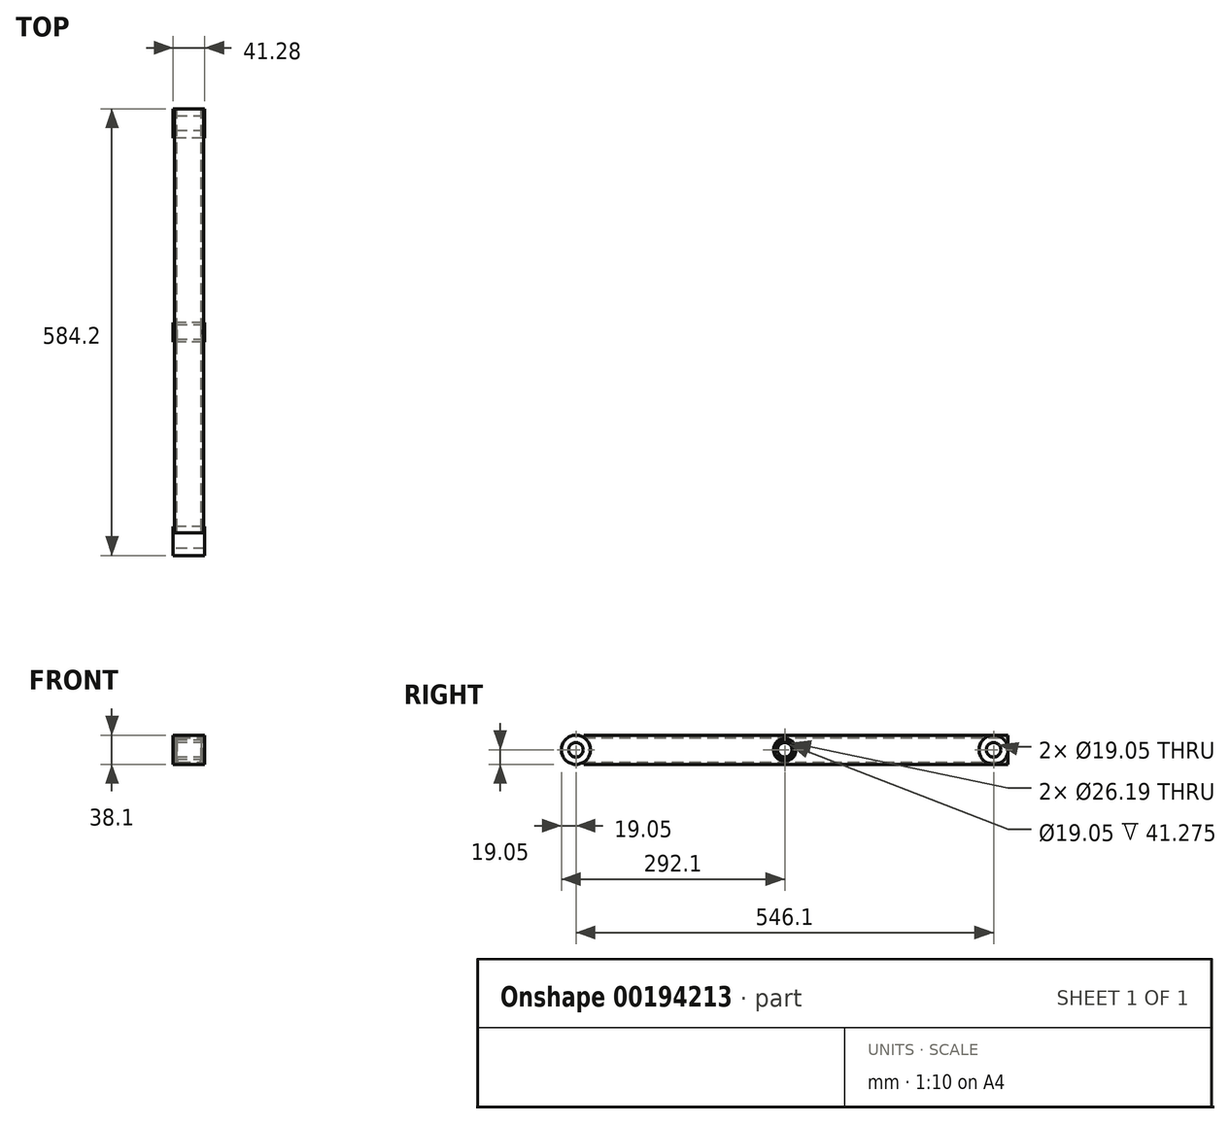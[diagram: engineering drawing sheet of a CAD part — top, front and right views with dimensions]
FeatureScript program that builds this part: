
annotation { "Feature Type Name" : "Feature", "Feature Type Description" : "" }
export const myFeature = defineFeature(function(context is Context, id is Id, definition is map)
    precondition{}
    {
        {
            var Q0;
            Q0=qCreatedBy(makeId("Front.planeOp"),FACE);
            var sketch = newSketch(context, id + "F0", { "sketchPlane" : qUnion([Q0])});
            skLineSegment(sketch, "E0.bottom", {"start": v(-19.05, 19.05) * mm, "end": v(19.05, 19.05) * mm});
            skLineSegment(sketch, "E0.top", {"start": v(-19.05, -19.05) * mm, "end": v(19.05, -19.05) * mm});
            skLineSegment(sketch, "E0.left", {"start": v(-19.05, 19.05) * mm, "end": v(-19.05, -19.05) * mm});
            skLineSegment(sketch, "E0.right", {"start": v(19.05, 19.05) * mm, "end": v(19.05, -19.05) * mm});
            skPoint(sketch, "E0.middle", {"position": v(0, 0) * mm});
            skLineSegment(sketch, "E1.bottom", {"start": v(-15.88, 15.88) * mm, "end": v(15.88, 15.88) * mm});
            skLineSegment(sketch, "E1.top", {"start": v(-15.88, -15.88) * mm, "end": v(15.88, -15.88) * mm});
            skLineSegment(sketch, "E1.left", {"start": v(-15.88, 15.88) * mm, "end": v(-15.88, -15.88) * mm});
            skLineSegment(sketch, "E1.right", {"start": v(15.88, 15.88) * mm, "end": v(15.88, -15.88) * mm});
            skSolve(sketch);
        }
        {
            var Q0;
            Q0=makeQuery(id+"F0.imprint","IMPRINT",FACE,{"disambiguationData":[TD([[makeQuery(id+"F0.imprint","IMPRINT",EDGE,{"derivedFrom":sQuery(id+"F0.wireOp",EDGE,"E0.bottom")}),-1.0]])]});
            extrude(context, id + "F1", {"entities" : qUnion([Q0]), "endBound" : BoundingType.SYMMETRIC, "depth" : 584.2 * mm});
        }
        {
            var Q0;
            Q0=makeQuery(id+"F1.opExtrude","SWEPT_EDGE",EDGE,{"disambiguationData":[OSD([sQuery(id+"F0.wireOp",EDGE,"E1.top"),sQuery(id+"F0.wireOp",EDGE,"E1.left")])]});
            var Q1;
            Q1=makeQuery(id+"F1.opExtrude","SWEPT_EDGE",EDGE,{"disambiguationData":[OSD([sQuery(id+"F0.wireOp",EDGE,"E1.top"),sQuery(id+"F0.wireOp",EDGE,"E1.right")])]});
            var Q2;
            Q2=makeQuery(id+"F1.opExtrude","SWEPT_EDGE",EDGE,{"disambiguationData":[OSD([sQuery(id+"F0.wireOp",EDGE,"E1.bottom"),sQuery(id+"F0.wireOp",EDGE,"E1.right")])]});
            var Q3;
            Q3=makeQuery(id+"F1.opExtrude","SWEPT_EDGE",EDGE,{"disambiguationData":[OSD([sQuery(id+"F0.wireOp",EDGE,"E1.bottom"),sQuery(id+"F0.wireOp",EDGE,"E1.left")])]});
            fillet(context, id + "F2", {"entities" : qUnion([Q0, Q1, Q2, Q3]), "radius" : 3.17 * mm, "tangentPropagation" : true, "allowEdgeOverflow" : false});
        }
        {
            var Q0;
            Q0=makeQuery(id+"F1.opExtrude","SWEPT_EDGE",EDGE,{"disambiguationData":[OSD([sQuery(id+"F0.wireOp",EDGE,"E0.top"),sQuery(id+"F0.wireOp",EDGE,"E0.left")])]});
            var Q1;
            Q1=makeQuery(id+"F1.opExtrude","SWEPT_EDGE",EDGE,{"disambiguationData":[OSD([sQuery(id+"F0.wireOp",EDGE,"E0.top"),sQuery(id+"F0.wireOp",EDGE,"E0.right")])]});
            var Q2;
            Q2=makeQuery(id+"F1.opExtrude","SWEPT_EDGE",EDGE,{"disambiguationData":[OSD([sQuery(id+"F0.wireOp",EDGE,"E0.bottom"),sQuery(id+"F0.wireOp",EDGE,"E0.right")])]});
            var Q3;
            Q3=makeQuery(id+"F1.opExtrude","SWEPT_EDGE",EDGE,{"disambiguationData":[OSD([sQuery(id+"F0.wireOp",EDGE,"E0.bottom"),sQuery(id+"F0.wireOp",EDGE,"E0.left")])]});
            fillet(context, id + "F3", {"entities" : qUnion([Q0, Q1, Q2, Q3]), "radius" : 6.35 * mm, "tangentPropagation" : true, "allowEdgeOverflow" : false});
        }
        {
            var Q0;
            Q0=qCreatedBy(makeId("Top.planeOp"),FACE);
            var sketch = newSketch(context, id + "F4", { "sketchPlane" : qUnion([Q0])});
            skLineSegment(sketch, "E2", {"start": v(-25.89, 0) * mm, "end": v(26.93, 0) * mm, "construction": true});
            skLineSegment(sketch, "E3", {"start": v(-19.05, 0) * mm, "end": v(19.05, 0) * mm});
            skLineSegment(sketch, "E4", {"start": v(19.05, 0) * mm, "end": v(19.05, 14.68) * mm});
            skLineSegment(sketch, "E5", {"start": v(19.05, 14.68) * mm, "end": v(17.46, 13.1) * mm});
            skLineSegment(sketch, "E6", {"start": v(17.46, 13.1) * mm, "end": v(-17.46, 13.1) * mm});
            skLineSegment(sketch, "E7", {"start": v(-17.46, 13.1) * mm, "end": v(-19.05, 14.68) * mm});
            skLineSegment(sketch, "E8", {"start": v(-19.05, 14.68) * mm, "end": v(-19.05, 0) * mm});
            skSolve(sketch);
        }
        {
            var Q0;
            Q0 = qSketchRegion(id + "F4", true);
            var Q1;
            Q1=sQuery(id+"F4.wireOp",EDGE,"E2");
            revolve(context, id + "F5", {"operationType" : NewBodyOperationType.REMOVE, "entities" : qUnion([Q0]), "axis" : qUnion([Q1]), "revolveType" : RevolveType.FULL, "oppositeDirection" : true});
        }
        {
            var Q0;
            {var subQ0=sQuery(id+"F0.wireOp",EDGE,"E0.right");var subQ1=sQuery(id+"F0.wireOp",EDGE,"E0.bottom");var subQ3=sQuery(id+"F4.wireOp",EDGE,"E5");var subQ4=sQuery(id+"F0.wireOp",EDGE,"E0.top");var subQ6=makeQuery(id+"F5.opRevolve","SWEPT_FACE",FACE,{"disambiguationData":[OSD([subQ3])]});Q0=makeQuery(id+"FDlItFZDn8p0pWP_1.1.F5.boolean.opBoolean","SPLIT",FACE,{"disambiguationData":[TD([makeQuery(id+"F5.boolean.opBoolean","COPY",FACE,{"derivedFrom":subQ6})])],"derivedFrom":makeQuery(id+"F5.boolean.opBoolean","SPLIT",FACE,{"disambiguationData":[TD([makeQuery(id+"F1.opExtrude","CAP_FACE",FACE,{"disambiguationData":[OSD([subQ1,subQ4,sQuery(id+"F0.wireOp",EDGE,"E0.left"),subQ0,sQuery(id+"F0.wireOp",EDGE,"E1.bottom"),sQuery(id+"F0.wireOp",EDGE,"E1.top"),sQuery(id+"F0.wireOp",EDGE,"E1.left"),sQuery(id+"F0.wireOp",EDGE,"E1.right")])],"isStart":true})])],"derivedFrom":makeQuery(id+"F1.opExtrude","SWEPT_FACE",FACE,{"disambiguationData":[OSD([subQ0])]})})});}
            var sketch = newSketch(context, id + "F6", { "sketchPlane" : qUnion([Q0])});
            skCircle(sketch, "E9", {"center": v(0, 0) * mm, "radius": 12.7 * mm});
            skCircle(sketch, "E10", {"center": v(0, 0) * mm, "radius": 9.53 * mm});
            skSolve(sketch);
        }
        {
            var Q0;
            Q0 = qSketchRegion(id + "F6", true);
            extrude(context, id + "F7", {"entities" : qUnion([Q0]), "depth" : 3.17 * mm, "hasSecondDirection" : true, "secondDirectionOppositeDirection" : true, "secondDirectionDepth" : 41.27 * mm});
        }
        {
            var Q0;
            {var subQ0=sQuery(id+"F0.wireOp",EDGE,"E0.right");var subQ1=sQuery(id+"F0.wireOp",EDGE,"E0.top");var subQ2=sQuery(id+"F0.wireOp",EDGE,"E0.bottom");Q0=makeQuery(id+"F5.boolean.opBoolean","SPLIT",FACE,{"disambiguationData":[TD([makeQuery(id+"F1.opExtrude","CAP_FACE",FACE,{"disambiguationData":[OSD([subQ2,subQ1,sQuery(id+"F0.wireOp",EDGE,"E0.left"),subQ0,sQuery(id+"F0.wireOp",EDGE,"E1.bottom"),sQuery(id+"F0.wireOp",EDGE,"E1.top"),sQuery(id+"F0.wireOp",EDGE,"E1.left"),sQuery(id+"F0.wireOp",EDGE,"E1.right")])],"isStart":false})])],"derivedFrom":makeQuery(id+"F1.opExtrude","SWEPT_FACE",FACE,{"disambiguationData":[OSD([subQ0])]})});}
            var sketch = newSketch(context, id + "F8", { "sketchPlane" : qUnion([Q0])});
            skLineSegment(sketch, "E11", {"start": v(-292.1, 19.05) * mm, "end": v(-262.52, 19.05) * mm});
            skLineSegment(sketch, "E12", {"start": v(-262.52, 19.05) * mm, "end": v(-262.52, 15.88) * mm});
            skLineSegment(sketch, "E13", {"start": v(-262.52, -15.87) * mm, "end": v(-262.52, -19.05) * mm});
            skLineSegment(sketch, "E14", {"start": v(-262.52, -19.05) * mm, "end": v(-292.1, -19.05) * mm});
            skArc(sketch, "E15.trimOffspring", {"start": v(-262.52, -15.87) * mm, "mid": v(-254, 0) * mm, "end": v(-262.52, 15.87) * mm});
            skLineSegment(sketch, "E16", {"start": v(-292.1, -19.05) * mm, "end": v(-292.1, 19.05) * mm});
            skSolve(sketch);
        }
        {
            var Q0;
            Q0 = qSketchRegion(id + "F8", true);
            extrude(context, id + "F9", {"entities" : qUnion([Q0]), "operationType" : NewBodyOperationType.REMOVE, "endBound" : BoundingType.THROUGH_ALL, "oppositeDirection" : true, "depth" : 25.4 * mm});
        }
        {
            var Q0;
            {var subQ0=sQuery(id+"F0.wireOp",EDGE,"E0.right");var subQ1=sQuery(id+"F0.wireOp",EDGE,"E0.top");var subQ2=sQuery(id+"F0.wireOp",EDGE,"E0.bottom");Q0=makeQuery(id+"F5.boolean.opBoolean","SPLIT",FACE,{"disambiguationData":[TD([makeQuery(id+"F1.opExtrude","CAP_FACE",FACE,{"disambiguationData":[OSD([subQ2,subQ1,sQuery(id+"F0.wireOp",EDGE,"E0.left"),subQ0,sQuery(id+"F0.wireOp",EDGE,"E1.bottom"),sQuery(id+"F0.wireOp",EDGE,"E1.top"),sQuery(id+"F0.wireOp",EDGE,"E1.left"),sQuery(id+"F0.wireOp",EDGE,"E1.right")])],"isStart":false})])],"derivedFrom":makeQuery(id+"F1.opExtrude","SWEPT_FACE",FACE,{"disambiguationData":[OSD([subQ0])]})});}
            var sketch = newSketch(context, id + "F10", { "sketchPlane" : qUnion([Q0])});
            skCircle(sketch, "E17", {"center": v(-273.05, 0) * mm, "radius": 19.05 * mm});
            skCircle(sketch, "E18", {"center": v(-273.05, 0) * mm, "radius": 9.53 * mm});
            skSolve(sketch);
        }
        {
            var Q0;
            Q0 = qSketchRegion(id + "F10", true);
            extrude(context, id + "F11", {"entities" : qUnion([Q0]), "depth" : 3.17 * mm, "hasSecondDirection" : true, "secondDirectionOppositeDirection" : true, "secondDirectionDepth" : 41.27 * mm});
        }
        {
            var Q0;
            Q0=makeQuery(id+"F11.opExtrude","SWEPT_BODY",BODY,{"disambiguationData":[OSD([sQuery(id+"F10.wireOp",EDGE,"E17"),sQuery(id+"F10.wireOp",EDGE,"E18")])]});
            var Q1;
            Q1=qCreatedBy(makeId("Front.planeOp"),FACE);
            mirror(context, id + "F12", {"entities" : qUnion([Q0]), "mirrorPlane" : qUnion([Q1])});
        }
        {
            var Q0;
            Q0=makeQuery(id+"F1.opExtrude","SWEPT_FACE",FACE,{"disambiguationData":[OSD([sQuery(id+"F0.wireOp",EDGE,"E0.bottom")])]});
            var sketch = newSketch(context, id + "F13", { "sketchPlane" : qUnion([Q0])});
            skLineSegment(sketch, "E19.bottom", {"start": v(46.04, -304.8) * mm, "end": v(20.64, -304.8) * mm});
            skLineSegment(sketch, "E19.top", {"start": v(46.04, 304.8) * mm, "end": v(20.64, 304.8) * mm});
            skLineSegment(sketch, "E19.left", {"start": v(46.04, -304.8) * mm, "end": v(46.04, 304.8) * mm});
            skLineSegment(sketch, "E19.right", {"start": v(20.64, -304.8) * mm, "end": v(20.64, 304.8) * mm});
            skLineSegment(sketch, "E20.bottom", {"start": v(-46.04, -304.8) * mm, "end": v(-20.64, -304.8) * mm});
            skLineSegment(sketch, "E20.top", {"start": v(-46.04, 304.8) * mm, "end": v(-20.64, 304.8) * mm});
            skLineSegment(sketch, "E20.left", {"start": v(-46.04, -304.8) * mm, "end": v(-46.04, 304.8) * mm});
            skLineSegment(sketch, "E20.right", {"start": v(-20.64, -304.8) * mm, "end": v(-20.64, 304.8) * mm});
            skSolve(sketch);
        }
        {
            var Q0;
            Q0=makeQuery(id+"F13.imprint","IMPRINT",FACE,{"disambiguationData":[TD([[makeQuery(id+"F13.imprint","IMPRINT",EDGE,{"derivedFrom":sQuery(id+"F13.wireOp",EDGE,"E20.bottom")}),1.0]])]});
            var Q1;
            Q1=makeQuery(id+"F13.imprint","IMPRINT",FACE,{"disambiguationData":[TD([[makeQuery(id+"F13.imprint","IMPRINT",EDGE,{"derivedFrom":sQuery(id+"F13.wireOp",EDGE,"E19.bottom")}),-1.0]])]});
            extrude(context, id + "F14", {"entities" : qUnion([Q0, Q1]), "operationType" : NewBodyOperationType.REMOVE, "oppositeDirection" : true, "depth" : 50.8 * mm});
        }
    });
